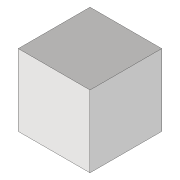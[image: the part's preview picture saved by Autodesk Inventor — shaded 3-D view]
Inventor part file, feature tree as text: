
AUTODESK INVENTOR PART (.ipt)
format: ipt  version: 2020 (Build 240168000, 168)  size: 73,216 bytes
history: native  units: mm
features: sketch x1, extrude x1
ambient origin geometry x8: Origin, YZ Plane, XZ Plane, XY Plane, X Axis, Y Axis, Z Axis, Center Point
bodies: Volumenkörper1 (feature_tree)
feature tree (2):
  sketch  "Skizze1"  dims[d0=1.0mm d1=1.0mm d3=0.0mm d4=1.0mm]
  extrude  "Extrusion1"  [1 undecoded]
note: 1 required parameter value undecoded (feature->parameter linkage not recoverable at this tier; creation-order binding heuristic only, values carry confidence <= 0.55)
